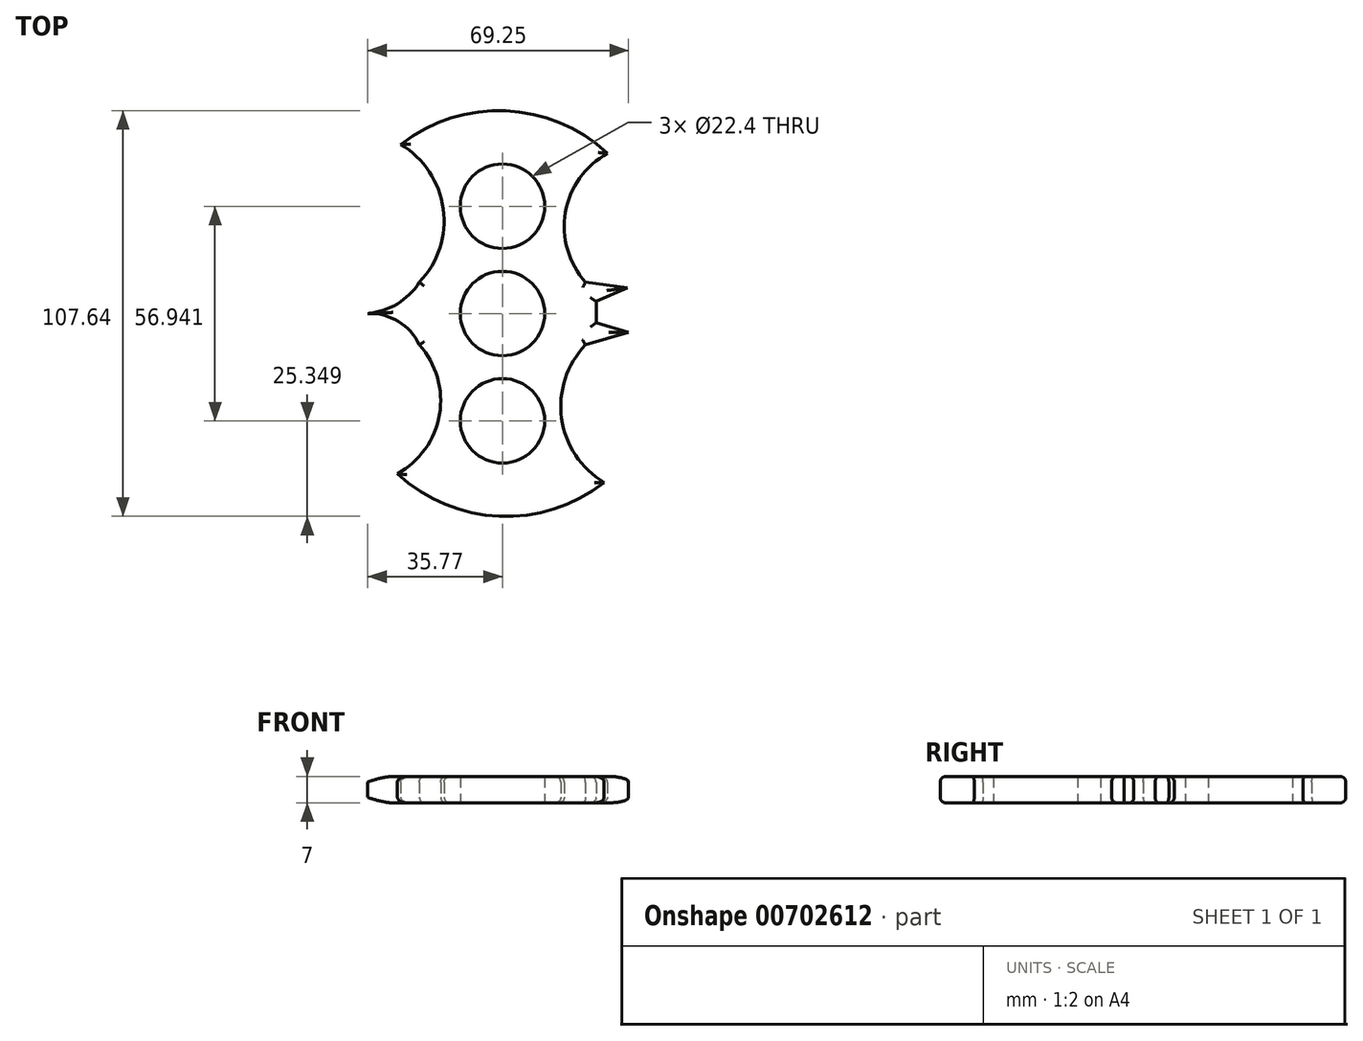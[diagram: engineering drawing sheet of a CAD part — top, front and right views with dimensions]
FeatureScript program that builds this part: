
annotation { "Feature Type Name" : "Feature", "Feature Type Description" : "" }
export const myFeature = defineFeature(function(context is Context, id is Id, definition is map)
    precondition{}
    {
        {
            var Q0;
            Q0=qCreatedBy(makeId("Top.planeOp"),FACE);
            var sketch = newSketch(context, id + "F0", { "sketchPlane" : qUnion([Q0])});
            skCircle(sketch, "E0", {"center": v(0, 0) * mm, "radius": 11.2 * mm});
            skCircle(sketch, "E1", {"center": v(0, 28.47) * mm, "radius": 11.2 * mm});
            skCircle(sketch, "E2.1.1", {"center": v(0, -28.47) * mm, "radius": 11.2 * mm});
            skArc(sketch, "E3", {"start": v(27.89, 42.49) * mm, "mid": v(0.87, 53.78) * mm, "end": v(-27.01, 44.82) * mm});
            skArc(sketch, "E4", {"start": v(-22.05, 8.32) * mm, "mid": v(-15.7, 27.77) * mm, "end": v(-27.01, 44.82) * mm});
            skArc(sketch, "E5.1.0", {"start": v(-27.89, -42.49) * mm, "mid": v(-0.87, -53.78) * mm, "end": v(27.01, -44.82) * mm});
            skArc(sketch, "E5.1.1", {"start": v(22.05, -8.32) * mm, "mid": v(15.7, -27.77) * mm, "end": v(27.01, -44.82) * mm});
            skArc(sketch, "E6", {"start": v(-35.77, 0) * mm, "mid": v(-27.93, 2.55) * mm, "end": v(-22.05, 8.32) * mm});
            skArc(sketch, "E7", {"start": v(27.89, 42.49) * mm, "mid": v(16.7, 26.82) * mm, "end": v(22.05, 8.32) * mm});
            skArc(sketch, "E8.1.0", {"start": v(-27.89, -42.49) * mm, "mid": v(-16.7, -26.82) * mm, "end": v(-22.05, -8.32) * mm});
            skArc(sketch, "E9", {"start": v(-22.05, -8.32) * mm, "mid": v(-27.64, -2.08) * mm, "end": v(-35.77, 0) * mm});
            skPoint(sketch, "E10.startSnap0", {"position": v(28.5, 6.86) * mm});
            skLineSegment(sketch, "E11", {"start": v(22.05, 8.32) * mm, "end": v(33.2, 6.86) * mm});
            skLineSegment(sketch, "E12", {"start": v(33.2, 6.86) * mm, "end": v(24.86, 3.22) * mm});
            skLineSegment(sketch, "E13", {"start": v(24.86, 3.22) * mm, "end": v(24.86, -2.44) * mm});
            skLineSegment(sketch, "E14", {"start": v(24.86, -2.44) * mm, "end": v(33.48, -5.03) * mm});
            skLineSegment(sketch, "E15", {"start": v(33.48, -5.03) * mm, "end": v(22.05, -8.32) * mm});
            skSolve(sketch);
        }
        {
            var Q0;
            Q0=makeQuery(id+"F0.imprint","IMPRINT",FACE,{"disambiguationData":[TD([[makeQuery(id+"F0.imprint","IMPRINT",EDGE,{"derivedFrom":sQuery(id+"F0.wireOp",EDGE,"E0")}),-1.0]])]});
            extrude(context, id + "F1", {"entities" : qUnion([Q0]), "depth" : 7 * mm, "offsetDistance" : 25 * mm});
        }
        {
            var Q0;
            Q0=makeQuery(id+"F1.opExtrude","CAP_EDGE",EDGE,{"disambiguationData":[OSD([sQuery(id+"F0.wireOp",EDGE,"E3")])],"isStart":false});
            var Q1;
            Q1=makeQuery(id+"F1.opExtrude","CAP_EDGE",EDGE,{"disambiguationData":[OSD([sQuery(id+"F0.wireOp",EDGE,"E7")])],"isStart":false});
            var Q2;
            Q2=makeQuery(id+"F1.opExtrude","CAP_EDGE",EDGE,{"disambiguationData":[OSD([sQuery(id+"F0.wireOp",EDGE,"E11")])],"isStart":false});
            var Q3;
            Q3=makeQuery(id+"F1.opExtrude","CAP_EDGE",EDGE,{"disambiguationData":[OSD([sQuery(id+"F0.wireOp",EDGE,"E15")])],"isStart":false});
            var Q4;
            Q4=makeQuery(id+"F1.opExtrude","CAP_EDGE",EDGE,{"disambiguationData":[OSD([sQuery(id+"F0.wireOp",EDGE,"E5.1.1")])],"isStart":false});
            var Q5;
            Q5=makeQuery(id+"F1.opExtrude","CAP_EDGE",EDGE,{"disambiguationData":[OSD([sQuery(id+"F0.wireOp",EDGE,"E13")])],"isStart":false});
            var Q6;
            Q6=makeQuery(id+"F1.opExtrude","CAP_EDGE",EDGE,{"disambiguationData":[OSD([sQuery(id+"F0.wireOp",EDGE,"E12")])],"isStart":false});
            var Q7;
            Q7=makeQuery(id+"F1.opExtrude","CAP_EDGE",EDGE,{"disambiguationData":[OSD([sQuery(id+"F0.wireOp",EDGE,"E14")])],"isStart":false});
            var Q8;
            Q8=makeQuery(id+"F1.opExtrude","CAP_EDGE",EDGE,{"disambiguationData":[OSD([sQuery(id+"F0.wireOp",EDGE,"E5.1.0")])],"isStart":false});
            var Q9;
            Q9=makeQuery(id+"F1.opExtrude","CAP_EDGE",EDGE,{"disambiguationData":[OSD([sQuery(id+"F0.wireOp",EDGE,"E4")])],"isStart":false});
            var Q10;
            Q10=makeQuery(id+"F1.opExtrude","CAP_EDGE",EDGE,{"disambiguationData":[OSD([sQuery(id+"F0.wireOp",EDGE,"E9")])],"isStart":false});
            var Q11;
            Q11=makeQuery(id+"F1.opExtrude","CAP_EDGE",EDGE,{"disambiguationData":[OSD([sQuery(id+"F0.wireOp",EDGE,"E8.1.0")])],"isStart":false});
            var Q12;
            Q12=makeQuery(id+"F1.opExtrude","CAP_EDGE",EDGE,{"disambiguationData":[OSD([sQuery(id+"F0.wireOp",EDGE,"E6")])],"isStart":false});
            fillet(context, id + "F2", {"entities" : qUnion([Q0, Q1, Q2, Q3, Q4, Q5, Q6, Q7, Q8, Q9, Q10, Q11, Q12]), "radius" : 1.5 * mm, "tangentPropagation" : true, "allowEdgeOverflow" : false});
        }
        {
            var Q0;
            Q0=makeQuery(id+"F1.opExtrude","CAP_EDGE",EDGE,{"disambiguationData":[OSD([sQuery(id+"F0.wireOp",EDGE,"E3")])],"isStart":true});
            var Q1;
            Q1=makeQuery(id+"F1.opExtrude","CAP_EDGE",EDGE,{"disambiguationData":[OSD([sQuery(id+"F0.wireOp",EDGE,"E11")])],"isStart":true});
            var Q2;
            Q2=makeQuery(id+"F1.opExtrude","CAP_EDGE",EDGE,{"disambiguationData":[OSD([sQuery(id+"F0.wireOp",EDGE,"E5.1.1")])],"isStart":true});
            var Q3;
            Q3=makeQuery(id+"F1.opExtrude","CAP_EDGE",EDGE,{"disambiguationData":[OSD([sQuery(id+"F0.wireOp",EDGE,"E15")])],"isStart":true});
            var Q4;
            Q4=makeQuery(id+"F1.opExtrude","CAP_EDGE",EDGE,{"disambiguationData":[OSD([sQuery(id+"F0.wireOp",EDGE,"E12")])],"isStart":true});
            var Q5;
            Q5=makeQuery(id+"F1.opExtrude","CAP_EDGE",EDGE,{"disambiguationData":[OSD([sQuery(id+"F0.wireOp",EDGE,"E14")])],"isStart":true});
            var Q6;
            Q6=makeQuery(id+"F1.opExtrude","CAP_EDGE",EDGE,{"disambiguationData":[OSD([sQuery(id+"F0.wireOp",EDGE,"E13")])],"isStart":true});
            var Q7;
            Q7=makeQuery(id+"F1.opExtrude","CAP_EDGE",EDGE,{"disambiguationData":[OSD([sQuery(id+"F0.wireOp",EDGE,"E6")])],"isStart":true});
            var Q8;
            Q8=makeQuery(id+"F1.opExtrude","CAP_EDGE",EDGE,{"disambiguationData":[OSD([sQuery(id+"F0.wireOp",EDGE,"E4")])],"isStart":true});
            var Q9;
            Q9=makeQuery(id+"F1.opExtrude","CAP_EDGE",EDGE,{"disambiguationData":[OSD([sQuery(id+"F0.wireOp",EDGE,"E9")])],"isStart":true});
            var Q10;
            Q10=makeQuery(id+"F1.opExtrude","CAP_EDGE",EDGE,{"disambiguationData":[OSD([sQuery(id+"F0.wireOp",EDGE,"E8.1.0")])],"isStart":true});
            var Q11;
            Q11=makeQuery(id+"F1.opExtrude","CAP_EDGE",EDGE,{"disambiguationData":[OSD([sQuery(id+"F0.wireOp",EDGE,"E7")])],"isStart":true});
            var Q12;
            Q12=makeQuery(id+"F1.opExtrude","CAP_EDGE",EDGE,{"disambiguationData":[OSD([sQuery(id+"F0.wireOp",EDGE,"E5.1.0")])],"isStart":true});
            fillet(context, id + "F3", {"entities" : qUnion([Q0, Q1, Q2, Q3, Q4, Q5, Q6, Q7, Q8, Q9, Q10, Q11, Q12]), "radius" : 1.5 * mm, "tangentPropagation" : true, "allowEdgeOverflow" : false});
        }
    });
